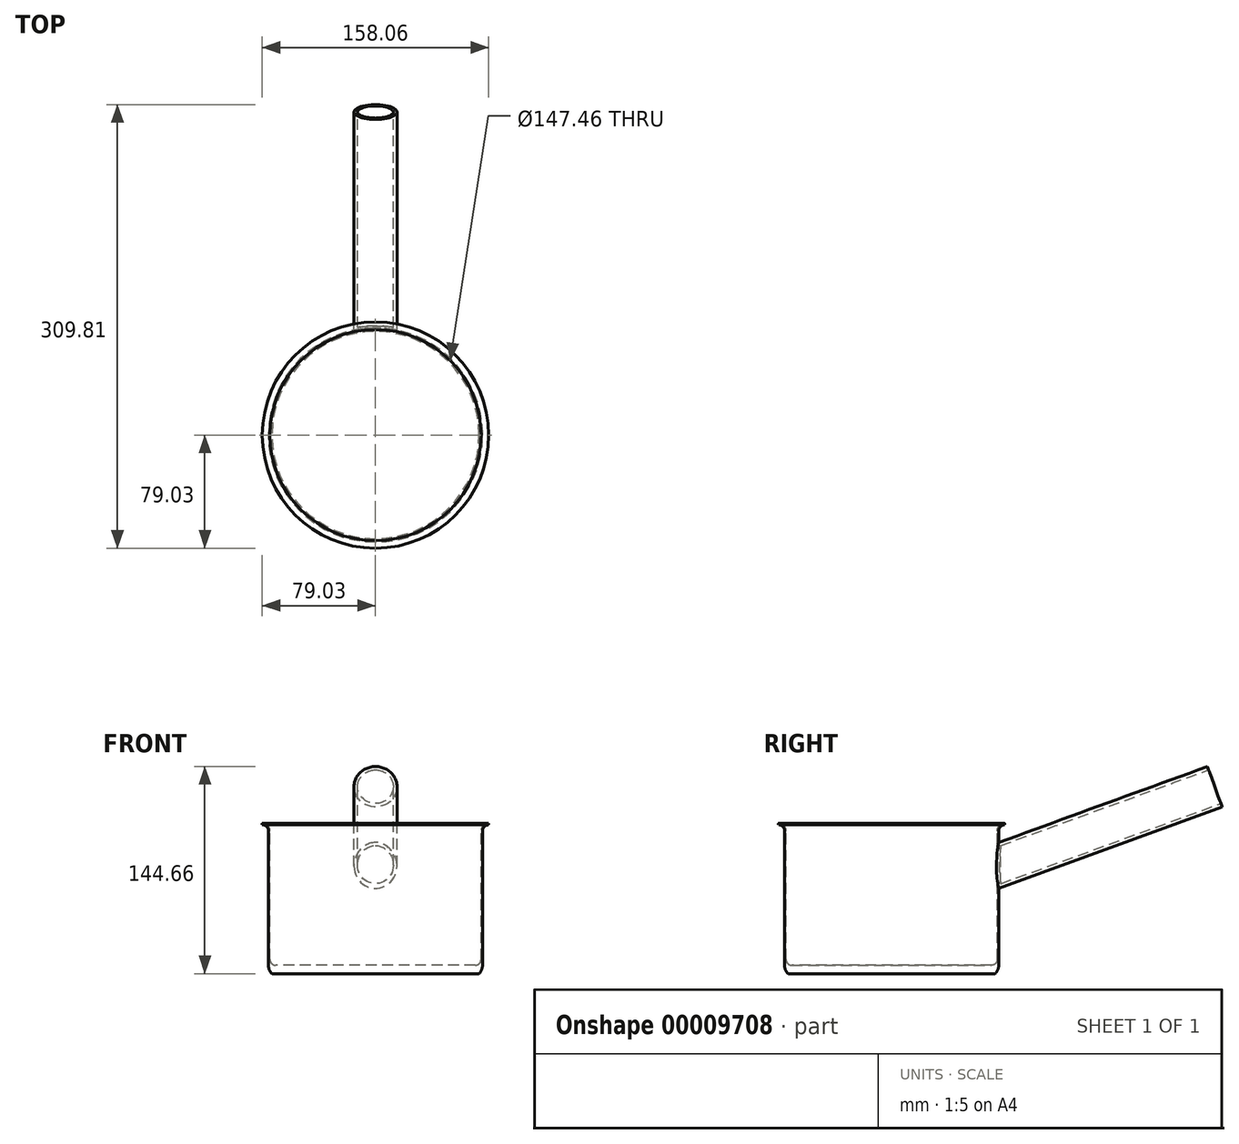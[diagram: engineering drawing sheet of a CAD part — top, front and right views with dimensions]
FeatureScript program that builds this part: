
annotation { "Feature Type Name" : "Feature", "Feature Type Description" : "" }
export const myFeature = defineFeature(function(context is Context, id is Id, definition is map)
    precondition{}
    {
        {
            var Q0;
            Q0=qCreatedBy(makeId("Front.planeOp"),FACE);
            var sketch = newSketch(context, id + "F0", { "sketchPlane" : qUnion([Q0])});
            skLineSegment(sketch, "E0.bottom", {"start": v(-74.73, 51.25) * mm, "end": v(-73.73, 51.25) * mm});
            skLineSegment(sketch, "E0.left", {"start": v(-74.73, 51.25) * mm, "end": v(-74.73, -42.54) * mm});
            skLineSegment(sketch, "E0.right", {"start": v(-73.73, 51.25) * mm, "end": v(-73.73, -38.54) * mm});
            skArc(sketch, "E1", {"start": v(-74.73, 51.25) * mm, "mid": v(-75.99, 54.27) * mm, "end": v(-79.02, 55.5) * mm});
            skArc(sketch, "E2.0", {"start": v(-73.73, 51.25) * mm, "mid": v(-75.28, 54.98) * mm, "end": v(-79.03, 56.5) * mm});
            skLineSegment(sketch, "E3", {"start": v(-79.03, 56.5) * mm, "end": v(-79.02, 55.5) * mm});
            skLineSegment(sketch, "E4.bottom", {"start": v(-69.73, -42.54) * mm, "end": v(0, -42.54) * mm});
            skLineSegment(sketch, "E4.top", {"start": v(-72.35, -48.43) * mm, "end": v(0, -48.43) * mm});
            skLineSegment(sketch, "E4.right", {"start": v(0, -42.54) * mm, "end": v(0, -48.43) * mm});
            skArc(sketch, "E5", {"start": v(-74.73, -42.54) * mm, "mid": v(-74.11, -45.72) * mm, "end": v(-72.35, -48.43) * mm});
            skPoint(sketch, "E6.visualSharp", {"position": v(-73.73, -42.54) * mm});
            skArc(sketch, "E6.filletArc", {"start": v(-73.73, -38.54) * mm, "mid": v(-72.56, -41.37) * mm, "end": v(-69.73, -42.54) * mm});
            skSolve(sketch);
        }
        {
            var Q0;
            Q0 = qSketchRegion(id + "F0", true);
            var Q1;
            Q1=sQuery(id+"F0.wireOp",EDGE,"E4.right");
            revolve(context, id + "F1", {"entities" : qUnion([Q0]), "axis" : qUnion([Q1]), "revolveType" : RevolveType.FULL});
        }
        {
            var Q0;
            Q0=sQuery(id+"F0.wireOp",EDGE,"E4.bottom");
            cPlane(context, id + "F2", {"entities" : qUnion([Q0]), "cplaneType" : CPlaneType.LINE_ANGLE, "offset" : 150 * mm, "angle" : 20 * degree, "width" : 150 * mm, "height" : 150 * mm});
        }
        {
            var Q0;
            Q0=qCreatedBy(id+"F2.planeOp",FACE);
            cPlane(context, id + "F3", {"entities" : qUnion([Q0]), "cplaneType" : CPlaneType.OFFSET, "offset" : 150 * mm, "width" : 150 * mm, "height" : 150 * mm});
        }
        {
            var Q0;
            Q0=qCreatedBy(id+"F3.planeOp",FACE);
            var sketch = newSketch(context, id + "F4", { "sketchPlane" : qUnion([Q0])});
            skCircle(sketch, "E7", {"center": v(0, 0) * mm, "radius": 15 * mm});
            skSolve(sketch);
        }
        {
            var Q0;
            Q0=makeQuery(id+"F4.imprint","IMPRINT",FACE,{"disambiguationData":[TD([[makeQuery(id+"F4.imprint","IMPRINT",EDGE,{"derivedFrom":sQuery(id+"F4.wireOp",EDGE,"E7")}),1.0]])]});
            extrude(context, id + "F5", {"entities" : qUnion([Q0]), "operationType" : NewBodyOperationType.ADD, "endBound" : BoundingType.UP_TO_NEXT, "oppositeDirection" : true, "depth" : 25 * mm, "hasSecondDirection" : true, "secondDirectionOppositeDirection" : false, "secondDirectionDepth" : 104.68 * mm});
        }
        {
            var Q0;
            Q0=makeQuery(id+"F5.opExtrude","CAP_FACE",FACE,{"disambiguationData":[OSD([sQuery(id+"F4.wireOp",EDGE,"E7")])],"isStart":true});
            shell(context, id + "F6", {"entities" : qUnion([Q0]), "thickness" : 2.5 * mm});
        }
    });
